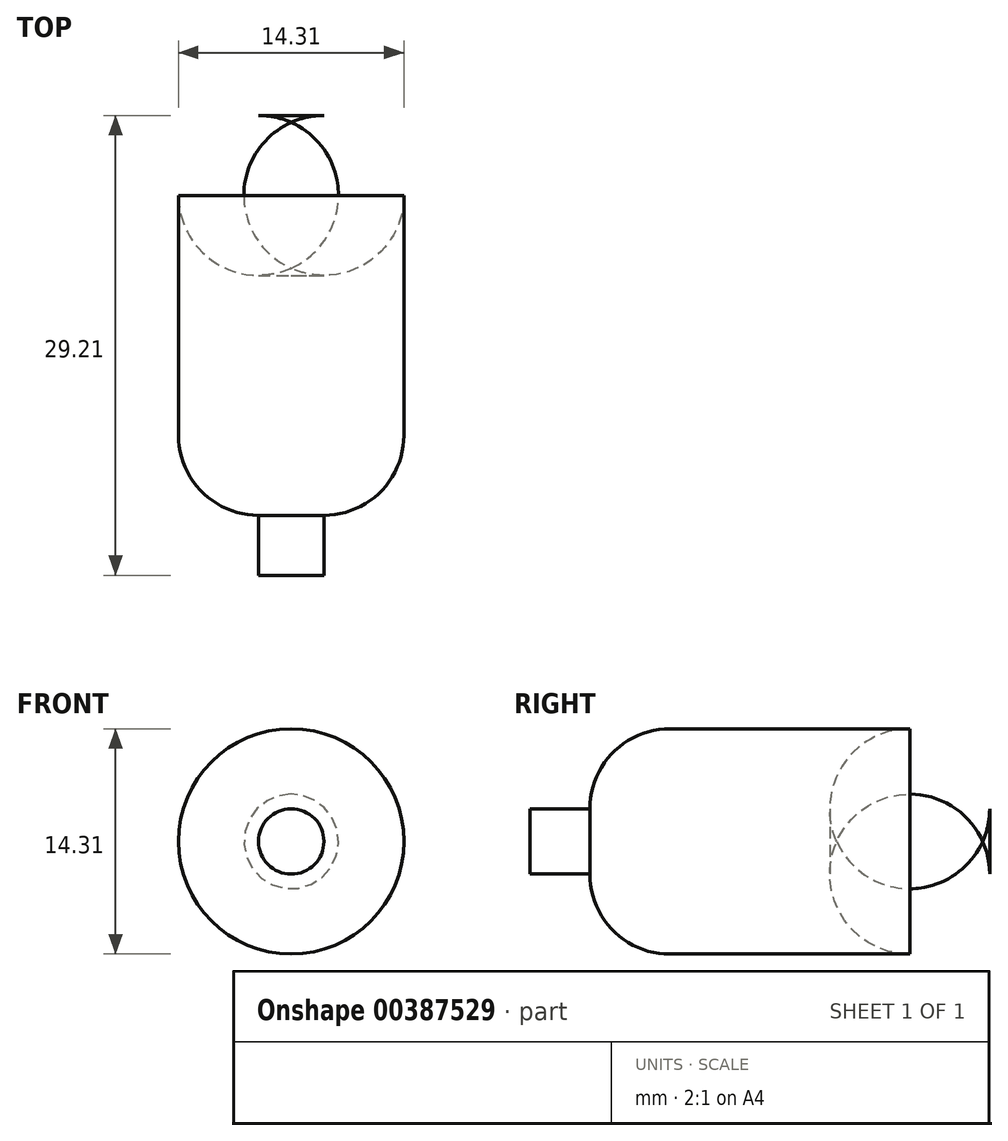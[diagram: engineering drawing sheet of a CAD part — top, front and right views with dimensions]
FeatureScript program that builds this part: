
annotation { "Feature Type Name" : "Feature", "Feature Type Description" : "" }
export const myFeature = defineFeature(function(context is Context, id is Id, definition is map)
    precondition{}
    {
        {
            var Q0;
            Q0=qCreatedBy(makeId("Front.planeOp"),FACE);
            var sketch = newSketch(context, id + "F0", { "sketchPlane" : qUnion([Q0])});
            skCircle(sketch, "E0", {"center": v(-65.16, 43.47) * mm, "radius": 7.16 * mm});
            skSolve(sketch);
        }
        {
            var Q0;
            Q0=makeQuery(id+"F0.imprint","IMPRINT",FACE,{"disambiguationData":[TD([[makeQuery(id+"F0.imprint","IMPRINT",EDGE,{"derivedFrom":sQuery(id+"F0.wireOp",EDGE,"E0")}),1.0]])]});
            extrude(context, id + "F1", {"entities" : qUnion([Q0]), "depth" : 25.4 * mm});
        }
        {
            var Q0;
            Q0=makeQuery(id+"F1.opExtrude","CAP_EDGE",EDGE,{"disambiguationData":[OSD([sQuery(id+"F0.wireOp",EDGE,"E0")])],"isStart":false});
            var Q1;
            Q1=makeQuery(id+"F1.opExtrude","CAP_EDGE",EDGE,{"disambiguationData":[OSD([sQuery(id+"F0.wireOp",EDGE,"E0")])],"isStart":true});
            fillet(context, id + "F2", {"entities" : qUnion([Q0, Q1]), "radius" : 5.08 * mm, "tangentPropagation" : true, "allowEdgeOverflow" : false});
        }
        {
            var Q0;
            Q0=makeQuery(id+"F1.opExtrude","CAP_FACE",FACE,{"disambiguationData":[OSD([sQuery(id+"F0.wireOp",EDGE,"E0")])],"isStart":false});
            extrude(context, id + "F3", {"entities" : qUnion([Q0]), "operationType" : NewBodyOperationType.ADD, "depth" : 3.8 * mm});
        }
    });
